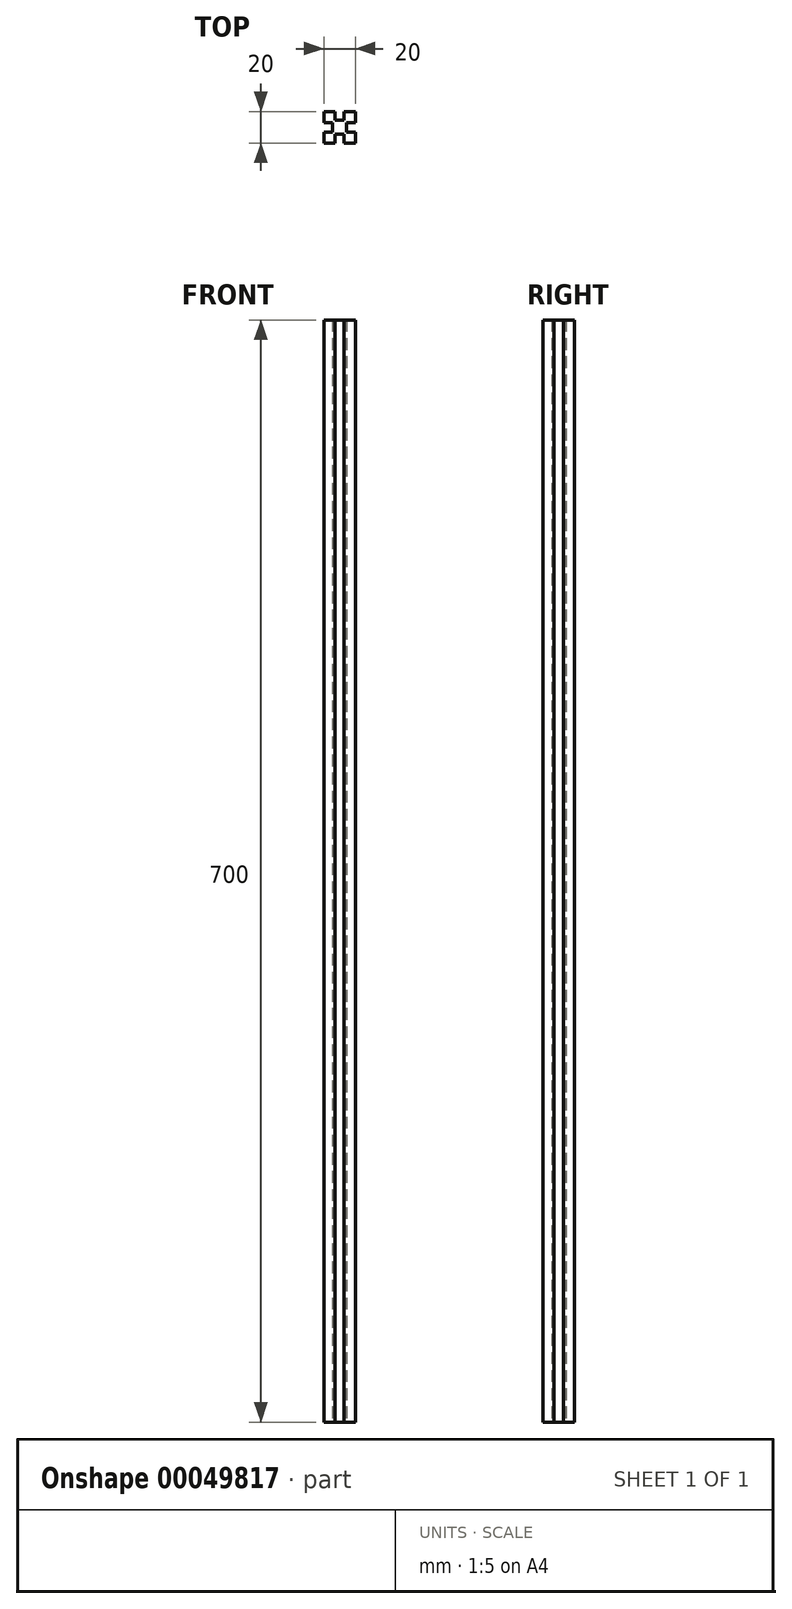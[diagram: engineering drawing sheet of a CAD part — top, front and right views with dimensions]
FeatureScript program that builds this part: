
annotation { "Feature Type Name" : "Feature", "Feature Type Description" : "" }
export const myFeature = defineFeature(function(context is Context, id is Id, definition is map)
    precondition{}
    {
        {
            var Q0;
            Q0=qCreatedBy(makeId("Top.planeOp"),FACE);
            var sketch = newSketch(context, id + "F0", { "sketchPlane" : qUnion([Q0])});
            skLineSegment(sketch, "E0.bottom", {"start": v(0, 0) * mm, "end": v(20, 0) * mm});
            skLineSegment(sketch, "E0.top", {"start": v(0, 20) * mm, "end": v(20, 20) * mm});
            skLineSegment(sketch, "E0.left", {"start": v(0, 0) * mm, "end": v(0, 20) * mm});
            skLineSegment(sketch, "E0.right", {"start": v(20, 0) * mm, "end": v(20, 20) * mm});
            skLineSegment(sketch, "E1.bottom", {"start": v(7, 20) * mm, "end": v(13, 20) * mm});
            skLineSegment(sketch, "E1.top", {"start": v(7, 14.5) * mm, "end": v(13, 14.5) * mm});
            skLineSegment(sketch, "E1.left", {"start": v(7, 20) * mm, "end": v(7, 14.5) * mm});
            skLineSegment(sketch, "E1.right", {"start": v(13, 20) * mm, "end": v(13, 14.5) * mm});
            skLineSegment(sketch, "E2.bottom", {"start": v(20, 13) * mm, "end": v(14.5, 13) * mm});
            skLineSegment(sketch, "E2.top", {"start": v(20, 7) * mm, "end": v(14.5, 7) * mm});
            skLineSegment(sketch, "E2.left", {"start": v(20, 13) * mm, "end": v(20, 7) * mm});
            skLineSegment(sketch, "E2.right", {"start": v(14.5, 13) * mm, "end": v(14.5, 7) * mm});
            skLineSegment(sketch, "E3.bottom", {"start": v(13, 0) * mm, "end": v(7, 0) * mm});
            skLineSegment(sketch, "E3.top", {"start": v(13, 5.5) * mm, "end": v(7, 5.5) * mm});
            skLineSegment(sketch, "E3.left", {"start": v(13, 0) * mm, "end": v(13, 5.5) * mm});
            skLineSegment(sketch, "E3.right", {"start": v(7, 0) * mm, "end": v(7, 5.5) * mm});
            skLineSegment(sketch, "E4.bottom", {"start": v(0, 7) * mm, "end": v(5.5, 7) * mm});
            skLineSegment(sketch, "E4.top", {"start": v(0, 13) * mm, "end": v(5.5, 13) * mm});
            skLineSegment(sketch, "E4.left", {"start": v(0, 7) * mm, "end": v(0, 13) * mm});
            skLineSegment(sketch, "E4.right", {"start": v(5.5, 7) * mm, "end": v(5.5, 13) * mm});
            skSolve(sketch);
        }
        {
            var Q0;
            Q0=makeQuery(id+"F0.imprint","IMPRINT",FACE,{"disambiguationData":[TD([[makeQuery(id+"F0.imprint","IMPRINT",EDGE,{"derivedFrom":sQuery(id+"F0.wireOp",EDGE,"E1.top")}),-1.0]])]});
            extrude(context, id + "F1", {"entities" : qUnion([Q0]), "depth" : 700 * mm});
        }
    });
